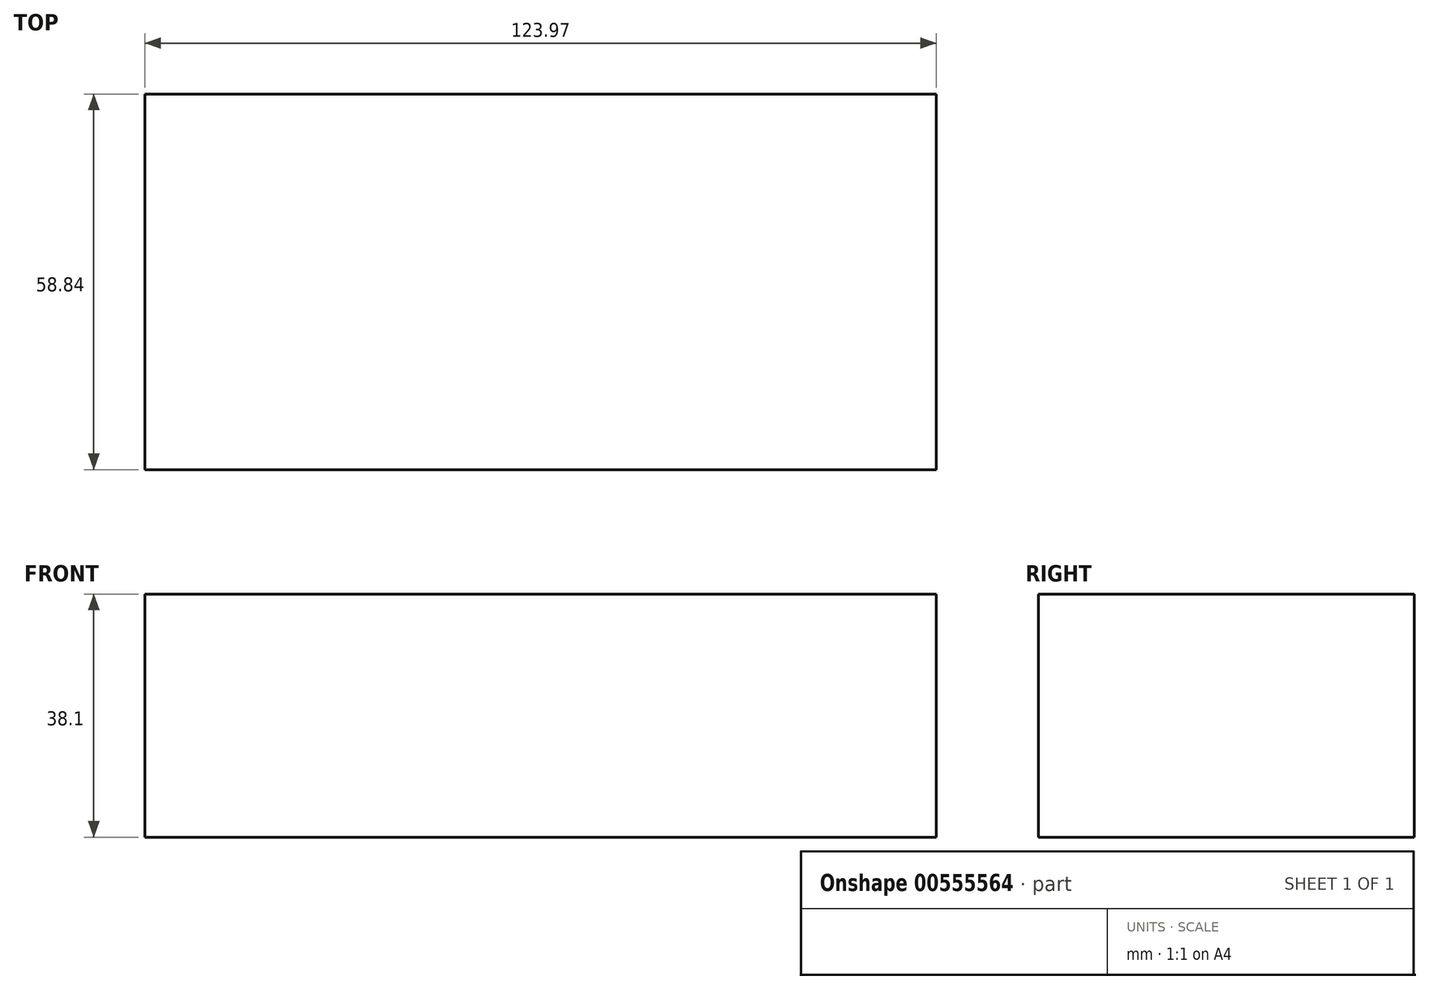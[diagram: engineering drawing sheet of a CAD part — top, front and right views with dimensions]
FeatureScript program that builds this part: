
annotation { "Feature Type Name" : "Feature", "Feature Type Description" : "" }
export const myFeature = defineFeature(function(context is Context, id is Id, definition is map)
    precondition{}
    {
        {
            var Q0;
            Q0=qCreatedBy(makeId("Top.planeOp"),FACE);
            var sketch = newSketch(context, id + "F0", { "sketchPlane" : qUnion([Q0])});
            skLineSegment(sketch, "E0.bottom", {"start": v(-59.66, 29.77) * mm, "end": v(64.31, 29.77) * mm});
            skLineSegment(sketch, "E0.top", {"start": v(-59.66, -29.07) * mm, "end": v(64.31, -29.07) * mm});
            skLineSegment(sketch, "E0.left", {"start": v(-59.66, 29.77) * mm, "end": v(-59.66, -29.07) * mm});
            skLineSegment(sketch, "E0.right", {"start": v(64.31, 29.77) * mm, "end": v(64.31, -29.07) * mm});
            skSolve(sketch);
        }
        {
            var Q0;
            Q0 = qSketchRegion(id + "F0", true);
            extrude(context, id + "F1", {"entities" : qUnion([Q0]), "depth" : 38.1 * mm, "offsetDistance" : 25.4 * mm});
        }
    });
